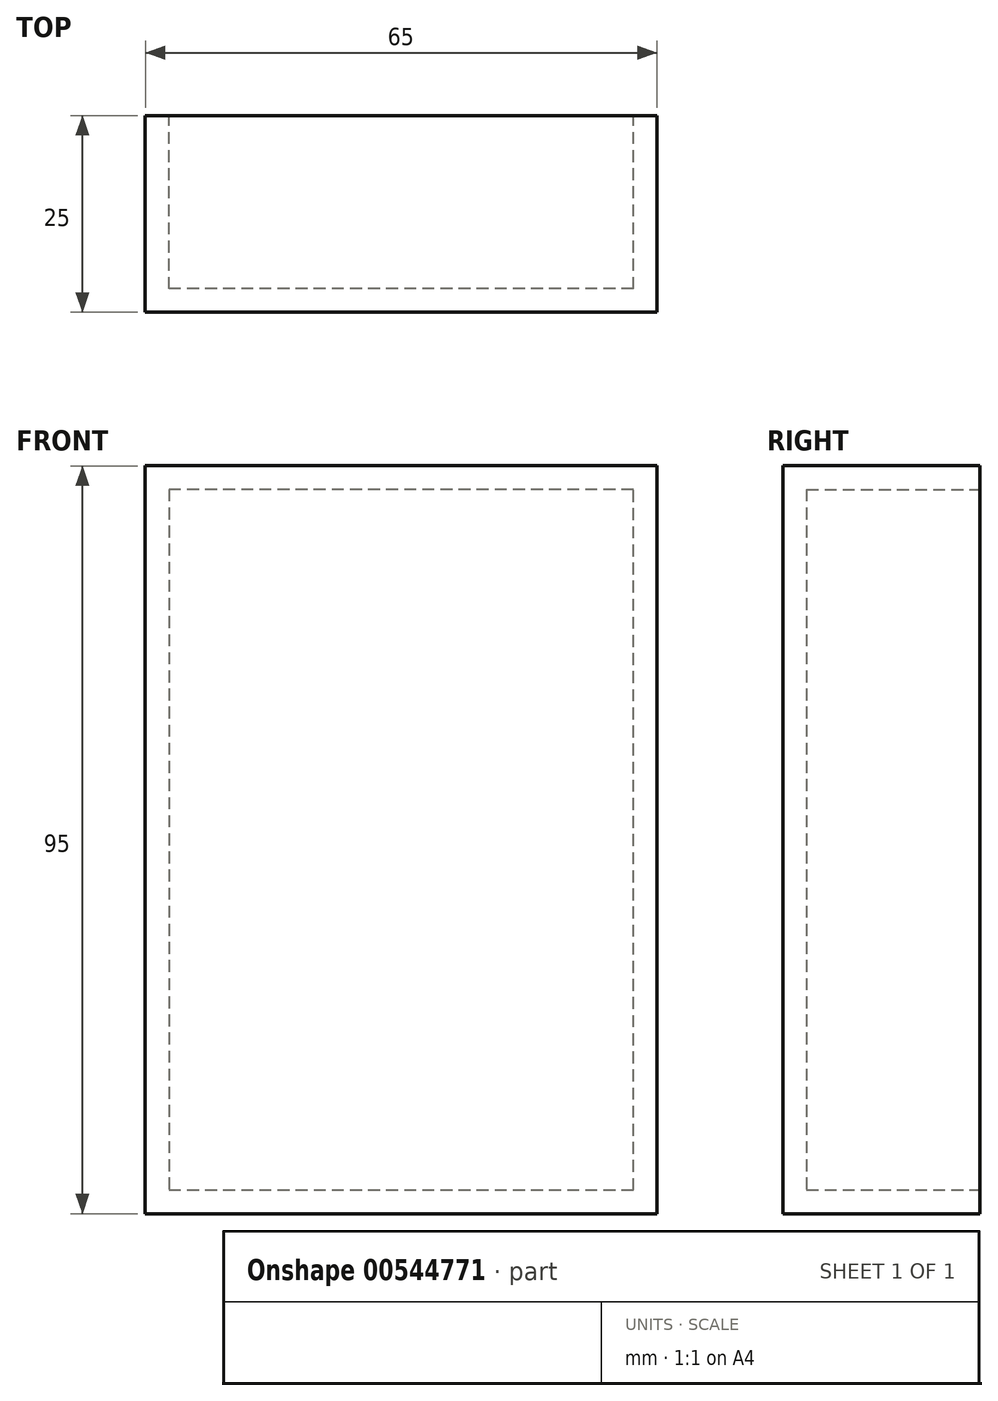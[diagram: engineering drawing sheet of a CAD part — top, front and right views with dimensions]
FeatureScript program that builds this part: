
annotation { "Feature Type Name" : "Feature", "Feature Type Description" : "" }
export const myFeature = defineFeature(function(context is Context, id is Id, definition is map)
    precondition{}
    {
        {
            var Q0;
            Q0=qCreatedBy(makeId("Front.planeOp"),FACE);
            var sketch = newSketch(context, id + "F0", { "sketchPlane" : qUnion([Q0])});
            skLineSegment(sketch, "E0", {"start": v(-40.58, 47.32) * mm, "end": v(-40.58, -47.68) * mm});
            skLineSegment(sketch, "E1", {"start": v(-40.58, -47.68) * mm, "end": v(24.42, -47.68) * mm});
            skLineSegment(sketch, "E2", {"start": v(24.42, -47.68) * mm, "end": v(24.42, 47.32) * mm});
            skLineSegment(sketch, "E3", {"start": v(24.42, 47.32) * mm, "end": v(-40.58, 47.32) * mm});
            skSolve(sketch);
        }
        {
            var Q0;
            Q0=makeQuery(id+"F0.imprint","IMPRINT",FACE,{"disambiguationData":[TD([[makeQuery(id+"F0.imprint","IMPRINT",EDGE,{"derivedFrom":sQuery(id+"F0.wireOp",EDGE,"E0")}),1.0]])]});
            extrude(context, id + "F1", {"entities" : qUnion([Q0]), "depth" : 25 * mm, "offsetDistance" : 25 * mm});
        }
        {
            var Q0;
            Q0=makeQuery(id+"F1.opExtrude","CAP_FACE",FACE,{"disambiguationData":[OSD([sQuery(id+"F0.wireOp",EDGE,"E0"),sQuery(id+"F0.wireOp",EDGE,"E1"),sQuery(id+"F0.wireOp",EDGE,"E2"),sQuery(id+"F0.wireOp",EDGE,"E3")])],"isStart":true});
            shell(context, id + "F2", {"entities" : qUnion([Q0]), "thickness" : 3 * mm});
        }
    });
